# Revit family: JC KONTAKTER JCK227 DE
name_source: partatom
category: Specialty Equipment
units: mm (PartAtom-declared; Revit-internal decimal feet)

## family parameters
Cut with Voids When Loaded = No
Enable Cutting in Views = Yes
Host = Face
Maintain Annotation Orientation = Yes
Part Type = Normal
Room Calculation Point = No
Round Connector Dimension = Use Diameter
Shared = No

## types (1)
- JCK227
    Anzahl der mikroschalter = 2
    CE-kennzeichnung = https://jckontakter.se
    Deckel = Aluminum ENAW 6060
    Deckel 2 = Aluminum ENAW 6060
    Default Elevation = 800 mm  [stored 2.62467 ft]
    Description = JCK227 gehört zu einer Serie von Großflächentastern mit doppelten Tastflächen, die es ermöglichen, z.B. eine zusätzliche Tür oder ein Schloss zu schalten. Der JCK227 ist aus silbereloxiertem Aluminium mit schwarzen Endkappen gefertigt. Beide Tastflächen sind mit vier taktilen Rillen versehen und dienen als zusätzliche Orientierungshilfe für sehbehinderte Personen. So lässt sich leicht erfühlen, wo man drücken muss, um die Türöffnung zu aktivieren.
    Endkappen = POM Tenac C 4520
    Geringster nennstrom = 1mA/4 V DC
    Herstellungsland = Schweden
    Kern = Aluminum ENAW 6060
    Kunststoffstück = POM Tenac C 4520
    Manufacturer = JC kontakter
    Mikroschalter = Standard NO IP67
    Model = JCK227
    Nomineller nennstrom = 12 V - Resistive 6A Inductive L/R 5ms 6A, 24 V - Resistive 6A Inductive L/R 5ms 5A
    Produktgewicht = 0.397 kg.
    Technisches Produktblatt = https://grossflaechentaster.de
    URL = https://grossflaechentaster.de

note: [stored X ft] marks values corroborated as IEEE doubles in the binary element streams (Revit-internal decimal feet)

## geometry (parser evidence)
native form markers: Sweep x6
no freeform markers — native parametric forms only
